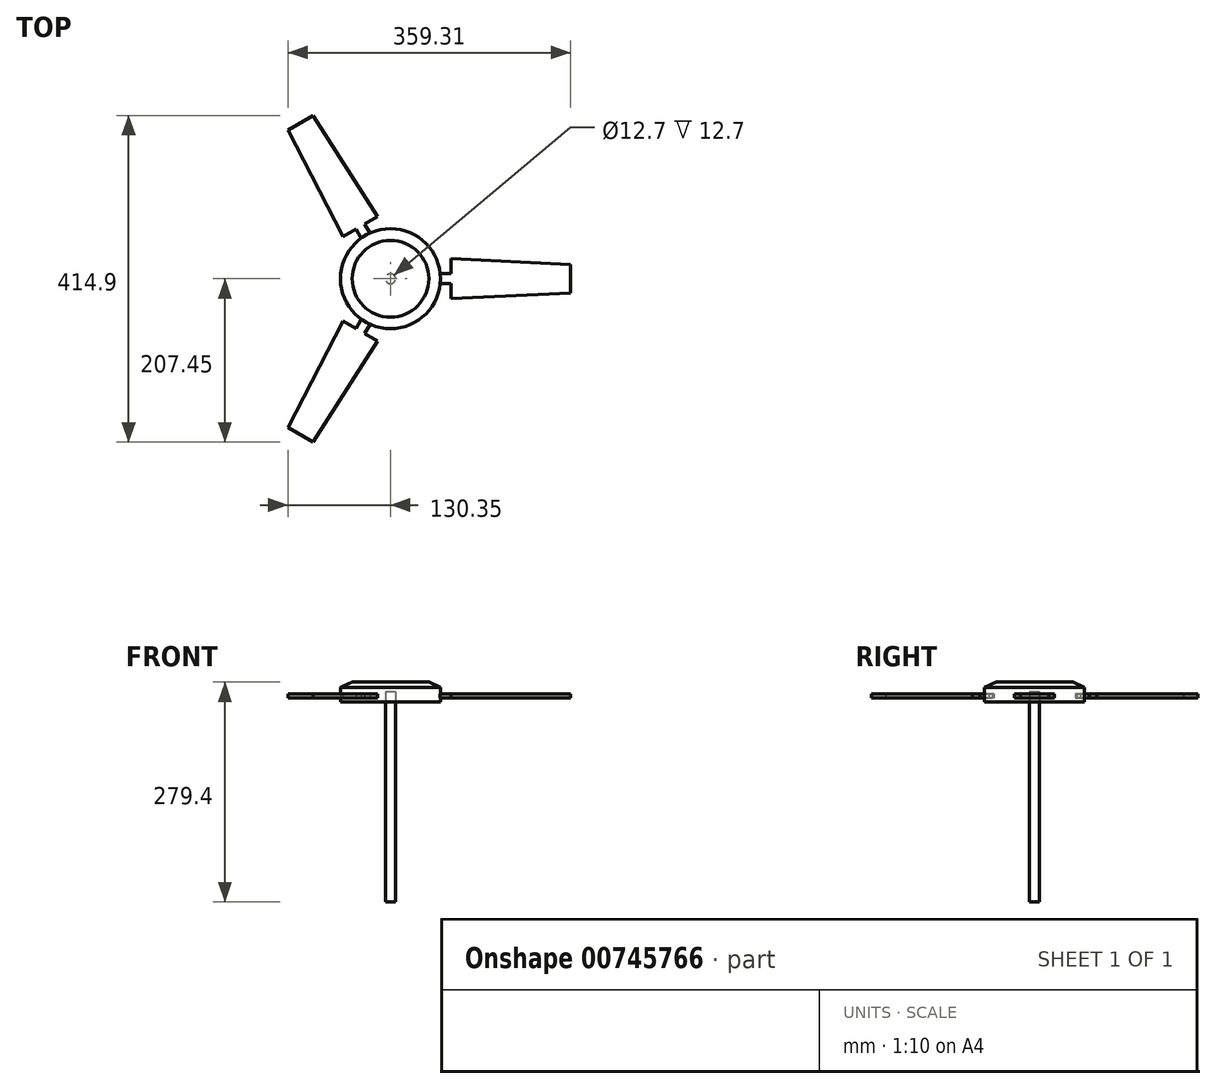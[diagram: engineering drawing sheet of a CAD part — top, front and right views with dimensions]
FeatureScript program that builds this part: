
annotation { "Feature Type Name" : "Feature", "Feature Type Description" : "" }
export const myFeature = defineFeature(function(context is Context, id is Id, definition is map)
    precondition{}
    {
        {
            var Q0;
            Q0=qCreatedBy(makeId("Top.planeOp"),FACE);
            var sketch = newSketch(context, id + "F0", { "sketchPlane" : qUnion([Q0])});
            skCircle(sketch, "E0", {"center": v(0, 0) * mm, "radius": 63.5 * mm});
            skSolve(sketch);
        }
        {
            var Q0;
            Q0=makeQuery(id+"F0.imprint","IMPRINT",FACE,{"disambiguationData":[TD([[makeQuery(id+"F0.imprint","IMPRINT",EDGE,{"derivedFrom":sQuery(id+"F0.wireOp",EDGE,"E0")}),1.0]])]});
            extrude(context, id + "F1", {"entities" : qUnion([Q0]), "depth" : 25.4 * mm, "offsetDistance" : 25.4 * mm});
        }
        {
            var Q0;
            Q0=qCreatedBy(makeId("Front.planeOp"),FACE);
            var sketch = newSketch(context, id + "F2", { "sketchPlane" : qUnion([Q0])});
            skLineSegment(sketch, "E1", {"start": v(37.48, 30.33) * mm, "end": v(69.12, 16.46) * mm});
            skLineSegment(sketch, "E2", {"start": v(69.12, 16.46) * mm, "end": v(69.12, 45.06) * mm});
            skLineSegment(sketch, "E3", {"start": v(37.48, 30.33) * mm, "end": v(69.12, 45.06) * mm});
            skLineSegment(sketch, "E4", {"start": v(0, 62.4) * mm, "end": v(0, -44.64) * mm});
            skSolve(sketch);
        }
        {
            var Q0;
            Q0 = qSketchRegion(id + "F2", true);
            var Q1;
            Q1=sQuery(id+"F2.wireOp",EDGE,"E4");
            revolve(context, id + "F3", {"operationType" : NewBodyOperationType.REMOVE, "surfaceOperationType" : NewSurfaceOperationType.NEW, "entities" : qUnion([Q0]), "axis" : qUnion([Q1]), "revolveType" : RevolveType.FULL, "oppositeDirection" : true});
        }
        {
            var Q0;
            Q0=qCreatedBy(makeId("Top.planeOp"),FACE);
            cPlane(context, id + "F4", {"entities" : qUnion([Q0]), "cplaneType" : CPlaneType.OFFSET, "offset" : 5.08 * mm, "width" : 152.4 * mm, "height" : 152.4 * mm});
        }
        {
            var Q0;
            Q0=qCreatedBy(id+"F4.planeOp",FACE);
            var sketch = newSketch(context, id + "F5", { "sketchPlane" : qUnion([Q0])});
            skLineSegment(sketch, "E5", {"start": v(61.49, 6.35) * mm, "end": v(61.49, -6.35) * mm});
            skLineSegment(sketch, "E6", {"start": v(61.49, 6.35) * mm, "end": v(76.73, 6.35) * mm});
            skLineSegment(sketch, "E7", {"start": v(76.73, 6.35) * mm, "end": v(76.73, 25.4) * mm});
            skLineSegment(sketch, "E8.MirrorCS", {"start": v(76.73, -6.35) * mm, "end": v(76.73, -25.4) * mm});
            skLineSegment(sketch, "E9", {"start": v(76.73, 25.4) * mm, "end": v(228.96, 18.33) * mm});
            skLineSegment(sketch, "E10.MirrorCS", {"start": v(76.73, -25.4) * mm, "end": v(228.96, -18.33) * mm});
            skLineSegment(sketch, "E11", {"start": v(228.96, 18.33) * mm, "end": v(228.96, -18.33) * mm});
            skLineSegment(sketch, "E12", {"start": v(61.49, -6.35) * mm, "end": v(76.73, -6.35) * mm});
            skLineSegment(sketch, "E13.1.0", {"start": v(-25.24, -56.42) * mm, "end": v(-32.86, -69.62) * mm});
            skLineSegment(sketch, "E13.1.1", {"start": v(-25.24, -56.42) * mm, "end": v(-36.24, -50.07) * mm});
            skLineSegment(sketch, "E13.1.2", {"start": v(-36.24, -50.07) * mm, "end": v(-43.86, -63.27) * mm});
            skLineSegment(sketch, "E13.1.3", {"start": v(-60.36, -53.75) * mm, "end": v(-130.35, -189.12) * mm});
            skLineSegment(sketch, "E13.1.4", {"start": v(-43.86, -63.27) * mm, "end": v(-60.36, -53.75) * mm});
            skLineSegment(sketch, "E13.1.5", {"start": v(-32.86, -69.62) * mm, "end": v(-16.37, -79.15) * mm});
            skLineSegment(sketch, "E13.1.6", {"start": v(-16.37, -79.15) * mm, "end": v(-98.6, -207.45) * mm});
            skLineSegment(sketch, "E13.1.7", {"start": v(-98.6, -207.45) * mm, "end": v(-130.35, -189.12) * mm});
            skLineSegment(sketch, "E13.2.0", {"start": v(-36.24, 50.07) * mm, "end": v(-43.86, 63.27) * mm});
            skLineSegment(sketch, "E13.2.1", {"start": v(-36.24, 50.07) * mm, "end": v(-25.24, 56.42) * mm});
            skLineSegment(sketch, "E13.2.2", {"start": v(-25.24, 56.42) * mm, "end": v(-32.86, 69.62) * mm});
            skLineSegment(sketch, "E13.2.3", {"start": v(-16.37, 79.15) * mm, "end": v(-98.6, 207.45) * mm});
            skLineSegment(sketch, "E13.2.4", {"start": v(-32.86, 69.62) * mm, "end": v(-16.37, 79.15) * mm});
            skLineSegment(sketch, "E13.2.5", {"start": v(-43.86, 63.27) * mm, "end": v(-60.36, 53.75) * mm});
            skLineSegment(sketch, "E13.2.6", {"start": v(-60.36, 53.75) * mm, "end": v(-130.35, 189.12) * mm});
            skLineSegment(sketch, "E13.2.7", {"start": v(-130.35, 189.12) * mm, "end": v(-98.6, 207.45) * mm});
            skPoint(sketch, "E13.center", {"position": v(0, 0) * mm});
            skLineSegment(sketch, "E13.anchor1", {"start": v(0, 0) * mm, "end": v(76.73, -25.4) * mm, "construction": true});
            skLineSegment(sketch, "E13.anchor2", {"start": v(0, 0) * mm, "end": v(-16.37, 79.15) * mm, "construction": true});
            skSolve(sketch);
        }
        {
            var Q0;
            Q0=makeQuery(id+"F5.imprint","IMPRINT",FACE,{"disambiguationData":[TD([[makeQuery(id+"F5.imprint","IMPRINT",EDGE,{"derivedFrom":sQuery(id+"F5.wireOp",EDGE,"E5")}),1.0]])]});
            var Q1;
            Q1=makeQuery(id+"F5.imprint","IMPRINT",FACE,{"disambiguationData":[TD([[makeQuery(id+"F5.imprint","IMPRINT",EDGE,{"derivedFrom":sQuery(id+"F5.wireOp",EDGE,"E13.2.0")}),-1.0]])]});
            var Q2;
            Q2=makeQuery(id+"F5.imprint","IMPRINT",FACE,{"disambiguationData":[TD([[makeQuery(id+"F5.imprint","IMPRINT",EDGE,{"derivedFrom":sQuery(id+"F5.wireOp",EDGE,"E13.1.0")}),-1.0]])]});
            extrude(context, id + "F6", {"entities" : qUnion([Q0, Q1, Q2]), "operationType" : NewBodyOperationType.ADD, "depth" : 5.08 * mm, "offsetDistance" : 25.4 * mm});
        }
        {
            var Q0;
            Q0=qCreatedBy(makeId("Top.planeOp"),FACE);
            var sketch = newSketch(context, id + "F7", { "sketchPlane" : qUnion([Q0])});
            skCircle(sketch, "E14", {"center": v(0, 0) * mm, "radius": 6.35 * mm});
            skSolve(sketch);
        }
        {
            var Q0;
            Q0 = qSketchRegion(id + "F7", true);
            extrude(context, id + "F8", {"entities" : qUnion([Q0]), "oppositeDirection" : true, "depth" : 254 * mm, "offsetDistance" : 25.4 * mm});
        }
        {
            var Q0;
            Q0 = qSketchRegion(id + "F7", true);
            extrude(context, id + "F9", {"entities" : qUnion([Q0]), "operationType" : NewBodyOperationType.REMOVE, "depth" : 12.7 * mm, "offsetDistance" : 25.4 * mm});
        }
    });
